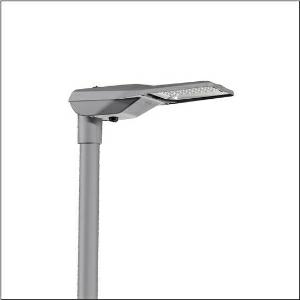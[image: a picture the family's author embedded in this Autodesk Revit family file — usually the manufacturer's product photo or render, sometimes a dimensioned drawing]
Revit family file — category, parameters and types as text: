
# Revit family: streetlight_sl_21_iq_mini___st1_0a_5xe2d21y08jb_5dbb
name_source: partatom
category: Lighting Fixtures
units: mm (PartAtom-declared; Revit-internal decimal feet)

## family parameters
Cut with Voids When Loaded = No
Host = Face
Light Source = No
Part Type = Normal
Room Calculation Point = No
Round Connector Dimension = Use Diameter
Shared = No

## types (1)
- --- (1 x LED, 9000 lm, 72.5 W, 2200K)
    Apparent Load = 73 VA
    CIE Flux Codes = 40 73 97 100 100
    Color Rendering = 70
    Color Temperature = 2200K
    Default Elevation = 1800 mm
    Description = Streetlight SL 21 iQ mini, mast luminaire, primary light control with lens, of PMMA, primary optical cover: cover, of toughened safety glass, transparent, light distribution: ST1.0a, light emission: direct distribution, primary light characteristic: asymmetric, installation type: post-top, side-entry, LED, High Power LED, rated luminous flux: 9.000lm, luminous efficacy: 124lm/W, light colour: 722, colour temperature: 2200K, control gear: iQ-Street Remote, D4i with power reduction, control: pre-setting: logarithmic dimming characteristic, Street-Remote, Auto-Match, Temp-Guard, Lumen-Switch, Night-Set, Smart-Wire, Light-Fading, Desk-Remote (wireless, voltage-free reading and setting of iQ features in the workshop via application-optimized NFC function/RFID function), optimised constant luminous flux control (CLO 2.0), mains connection: 220..240V, AC, 50/60Hz, start of lifetime: 73W, end of service life: 76W, reduction: 33W, luminaire housing, of diecast aluminium, powder-coated, SITECO metallic grey (DB 702S), corrosivity category C5 high according to DIN EN ISO 12944, please order mast flange separately, inclination adjustable: 0°, 5°, 10°, 15°, sealing non-destructively replaceable, multi-level sealing system, length: 628mm, width: 235mm, height: 110mm, mast flange for spigot size: 42mm (side-entry): 5XC10008XM4, 60/48mm (side-entry/post-top): 5XC10108XM2, 76/60mm (side-entry/post-top): 5XC10108XM1, mounting height: 4..8m, Smart Interface below and above, protection rating (complete): IP66, insulation class (complete): insulation class II (safety insulation), certification: CE, ENEC, ENEC+, VDE, impact resistance: IK10, permissible operating ambient temperature for outdoor applications: -40..+50°C, standard-compliant lighting for roads and squares, packaging unit: 1 piece

Light Distribution: ST1.0a
    Height = 110 mm
    Lamp = 1 x LED
    Lamp Light Flux = 9000 lm
    Lamp Power = 72.5 W
    Lamp count = 1
    Length = 625 mm
    Luminous efficacy = 124 lm/W
    Manufacturer = Siteco
    ModVariant = No
    Model = 5XE2D21Y08JB
    Number of Poles = 1
    OnlyDefault = Yes
    Power Factor = 1
    Product Name = Streetlight SL 21 iQ mini | ST1.0a
    Product group = mast luminaire | pylon top
    ProductGroupID = 6100
    Protection Class = Protection class II
    Protection Degree = IP 66
    RLX_Detail_Level = 1
    RLX_Emergency_Light_Flux = 0 lm
    RLX_Emergency_Type = 0
    RLX_Emergency_Type_DB = No
    RlxData = <blob elided: 92261 chars, md5=a59e517e>
    Socket = socket
    Standby Power = 0 W
    System Light Flux = 9000 lm
    System Power = 73 W
    Type Comments = factory setting: luminous flux: 100 % | dim-lin: 254 | 755 mA
    Type Image = l_1003514.jpg
    URL = http://relux.com
    VarID = @adj_114271
    Voltage = 0 V
    Weight = 0.00 kg
    Width = 234 mm

## geometry (parser evidence)
native form markers: Blend x4, Sweep x11
no freeform markers — native parametric forms only
